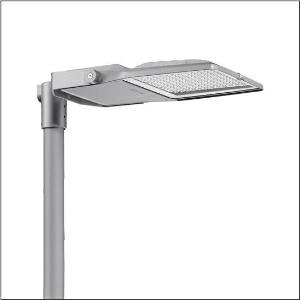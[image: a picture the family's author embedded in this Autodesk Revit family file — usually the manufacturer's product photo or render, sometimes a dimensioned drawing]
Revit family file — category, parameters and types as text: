
# Revit family: floodlight_fl_21_iq_midi___pl64_5xa7781e4e3a_69c6
name_source: partatom
category: Lighting Fixtures
units: mm (PartAtom-declared; Revit-internal decimal feet)

## family parameters
Cut with Voids When Loaded = No
Host = Face
Light Source = No
Part Type = Normal
Room Calculation Point = No
Round Connector Dimension = Use Diameter
Shared = No

## types (1)
- --- (1 x LED, 27050 lm, 208.1 W, 4000K)
    Apparent Load = 208 VA
    CIE Flux Codes = 28 80 98 100 100
    Color Rendering = 70
    Color Temperature = 4000K
    Default Elevation = 1800 mm
    Description = Floodlight FL 21 iQ midi, floodlight, primary light control with lens, of PMMA, primary optical cover: protective disc, of toughened safety glass, transparent, light distribution: PL64, light emission: direct distribution, installation type: surface-mounted, LED, High Power LED, rated luminous flux: 27.050lm, luminous efficacy: 130lm/W, light colour: 740, colour temperature: 4000K, control gear: ECG iQ, control: optimised constant luminous flux control (CLO 2.0), Desk-Remote (wireless, voltage-free reading and setting of iQ features in the workshop via application-optimized NFC function/RFID function), Light-Fading, Smart-Wire, Night-Set, Lumen-Switch, Temp-Guard, Auto-Match, with terminal, 6-pole, mains connection: 220..240V, AC, 50/60Hz, start of lifetime: 208W, end of service life: 227W, reduction: 90W, luminaire housing, of diecast aluminium, powder-coated, Siteco® metallic grey (DB 702S), corrosivity category C5 mid according to DIN EN ISO 12944, sealing non-destructively replaceable, please order mast flange separately, mast bracket, of steel, galvanised, powder-coated, Siteco® metallic grey (DB 702S), protection rating (complete): IP66, insulation class (complete): insulation class II (safety insulation), certification: CE, protection symbol: D, impact resistance: IK08, permissible operating ambient temperature: -40..+40°C, permissible operating ambient temperature for outdoor applications: -40..+50°C, standard: DIN EN 12944, LABS conformity tested according to VDMA 24364:2018-05, packaging unit: 1 piece

Light Distribution: PL64
    Height = 76 mm
    Lamp = 1 x LED
    Lamp Light Flux = 27050 lm
    Lamp Power = 208.1 W
    Lamp count = 1
    Length = 657 mm
    Luminous efficacy = 130 lm/W
    Manufacturer = Siteco
    ModVariant = No
    Model = 5XA7781E4E3A
    Number of Poles = 1
    OnlyDefault = Yes
    Power Factor = 1
    Product Name = Floodlight FL 21 iQ midi | PL64
    Product group = floodlight | pylon annexe
    ProductGroupID = 6200
    Protection Class = Protection class II
    Protection Degree = IP 66
    RLX_Detail_Level = 1
    RLX_Emergency_Light_Flux = 0 lm
    RLX_Emergency_Type = 0
    RLX_Emergency_Type_DB = No
    RlxData = <blob elided: 153573 chars, md5=eea3c126>
    Socket = socket
    Standby Power = 0 W
    System Light Flux = 27050 lm
    System Power = 208 W
    Type Comments = factory setting: luminous flux: 100 % | dim-lin: 254 | 710 mA
    Type Image = l_1007123.jpg
    URL = http://relux.com
    VarID = @adj_055495
    Voltage = 0 V
    Weight = 0.00 kg
    Width = 442 mm

## geometry (parser evidence)
native form markers: Blend x4, Sweep x13
no freeform markers — native parametric forms only
